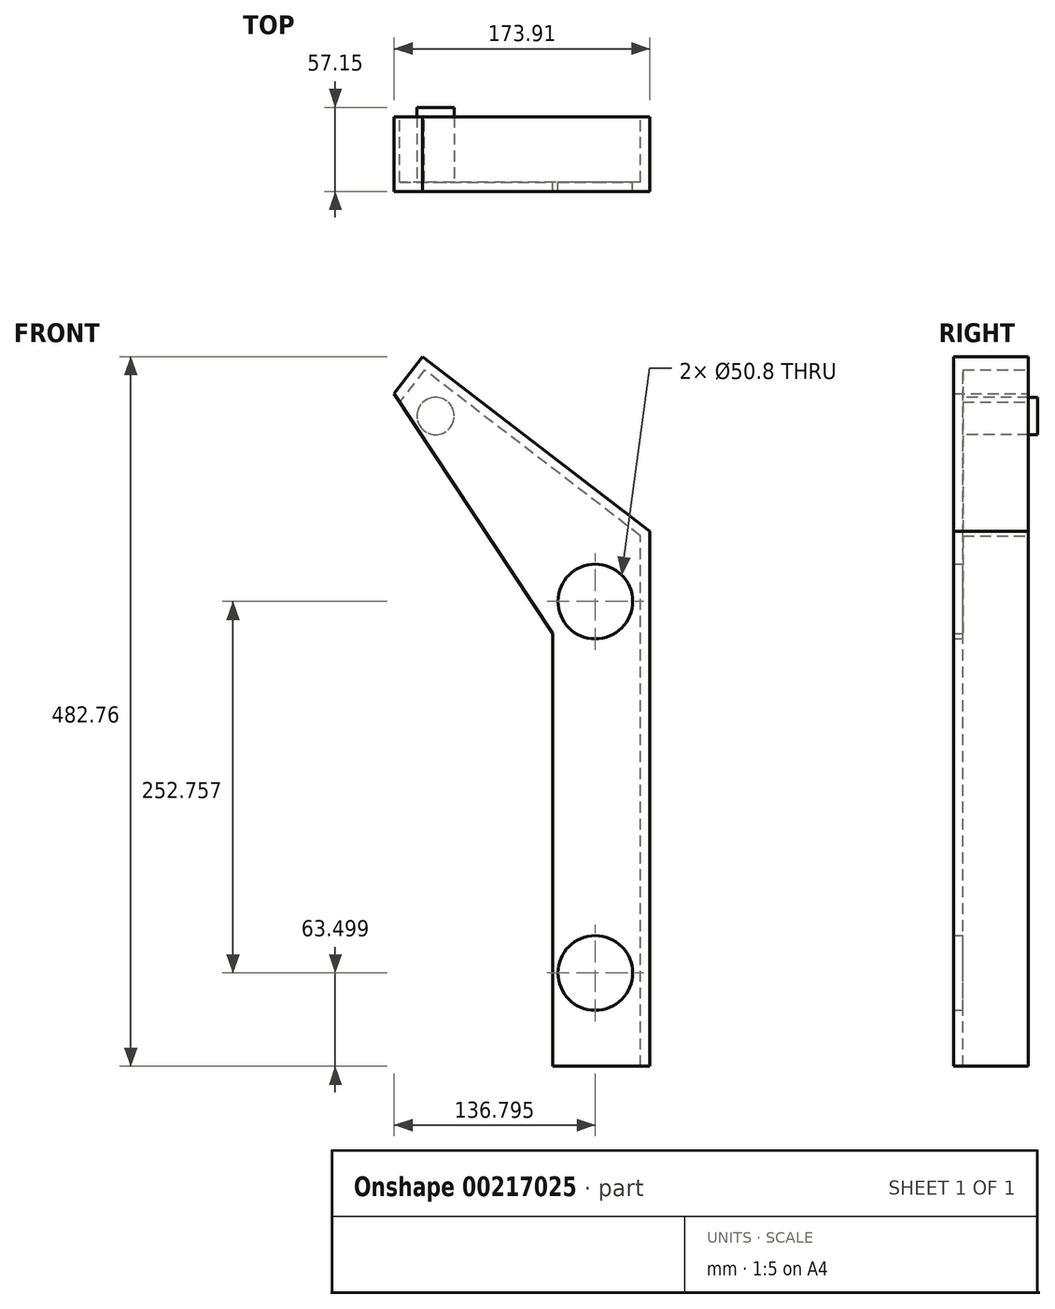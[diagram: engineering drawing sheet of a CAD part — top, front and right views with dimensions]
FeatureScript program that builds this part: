
annotation { "Feature Type Name" : "Feature", "Feature Type Description" : "" }
export const myFeature = defineFeature(function(context is Context, id is Id, definition is map)
    precondition{}
    {
        {
            var Q0;
            Q0=qCreatedBy(makeId("Front.planeOp"),FACE);
            var sketch = newSketch(context, id + "F0", { "sketchPlane" : qUnion([Q0])});
            skLineSegment(sketch, "E0.bottom", {"start": v(-258.74, -205.8) * mm, "end": v(-324.78, -205.8) * mm});
            skLineSegment(sketch, "E0.left", {"start": v(-258.74, -205.8) * mm, "end": v(-258.74, 158.24) * mm});
            skLineSegment(sketch, "E0.right", {"start": v(-324.78, -205.8) * mm, "end": v(-324.78, 88.58) * mm});
            skPoint(sketch, "E0.middle", {"position": v(-295.85, 110.46) * mm});
            skLineSegment(sketch, "E1", {"start": v(-258.74, 158.24) * mm, "end": v(-413.32, 276.96) * mm});
            skLineSegment(sketch, "E2", {"start": v(-413.32, 276.96) * mm, "end": v(-432.65, 251.78) * mm});
            skLineSegment(sketch, "E3", {"start": v(-432.65, 251.78) * mm, "end": v(-324.78, 88.58) * mm});
            skCircle(sketch, "E4", {"center": v(-295.85, 110.46) * mm, "radius": 25.4 * mm});
            skCircle(sketch, "E5", {"center": v(-295.85, -142.3) * mm, "radius": 25.4 * mm});
            skLineSegment(sketch, "E6.0", {"start": v(-412.15, 268.06) * mm, "end": v(-428.95, 246.18) * mm});
            skLineSegment(sketch, "E6.1", {"start": v(-265.09, 155.1) * mm, "end": v(-412.15, 268.06) * mm});
            skLineSegment(sketch, "E6.2", {"start": v(-265.09, -205.8) * mm, "end": v(-265.09, 155.1) * mm});
            skSolve(sketch);
        }
        {
            var Q0;
            {var subQ0=sQuery(id+"F0.wireOp",EDGE,"E0.right");Q0=makeQuery(id+"F0.imprint","IMPRINT",FACE,{"disambiguationData":[TD([[makeQuery(id+"F0.imprint","IMPRINT",EDGE,{"derivedFrom":subQ0}),-1.0]])]});}
            var Q1;
            {var subQ2=sQuery(id+"F0.wireOp",EDGE,"E0.left");Q1=makeQuery(id+"F0.imprint","IMPRINT",FACE,{"disambiguationData":[TD([[makeQuery(id+"F0.imprint","IMPRINT",EDGE,{"derivedFrom":subQ2}),1.0]])]});}
            extrude(context, id + "F1", {"entities" : qUnion([Q0, Q1]), "depth" : 50.8 * mm});
        }
        {
            var Q0;
            {var subQ0=sQuery(id+"F0.wireOp",EDGE,"E0.right");Q0=makeQuery(id+"F0.imprint","IMPRINT",FACE,{"disambiguationData":[TD([[makeQuery(id+"F0.imprint","IMPRINT",EDGE,{"derivedFrom":subQ0}),-1.0]])]});}
            extrude(context, id + "F2", {"entities" : qUnion([Q0]), "operationType" : NewBodyOperationType.REMOVE, "depth" : 44.45 * mm});
        }
        {
            var Q0;
            Q0=makeQuery(id+"F2.boolean.opBoolean","COPY",FACE,{"derivedFrom":makeQuery(id+"F2.opExtrude","CAP_FACE",FACE,{"disambiguationData":[OSD([sQuery(id+"F0.wireOp",EDGE,"E0.bottom"),sQuery(id+"F0.wireOp",EDGE,"E0.right"),sQuery(id+"F0.wireOp",EDGE,"E3"),sQuery(id+"F0.wireOp",EDGE,"E4"),sQuery(id+"F0.wireOp",EDGE,"E5"),sQuery(id+"F0.wireOp",EDGE,"E6.0"),sQuery(id+"F0.wireOp",EDGE,"E6.1"),sQuery(id+"F0.wireOp",EDGE,"E6.2")])],"isStart":false})});
            var sketch = newSketch(context, id + "F3", { "sketchPlane" : qUnion([Q0])});
            skCircle(sketch, "E7", {"center": v(404.48, 236.68) * mm, "radius": 12.7 * mm});
            skSolve(sketch);
        }
        {
            var Q0;
            Q0=makeQuery(id+"F3.imprint","IMPRINT",FACE,{"disambiguationData":[TD([[makeQuery(id+"F3.imprint","IMPRINT",EDGE,{"derivedFrom":sQuery(id+"F3.wireOp",EDGE,"E7")}),1.0]])]});
            extrude(context, id + "F4", {"entities" : qUnion([Q0]), "operationType" : NewBodyOperationType.ADD, "depth" : 50.8 * mm});
        }
    });
